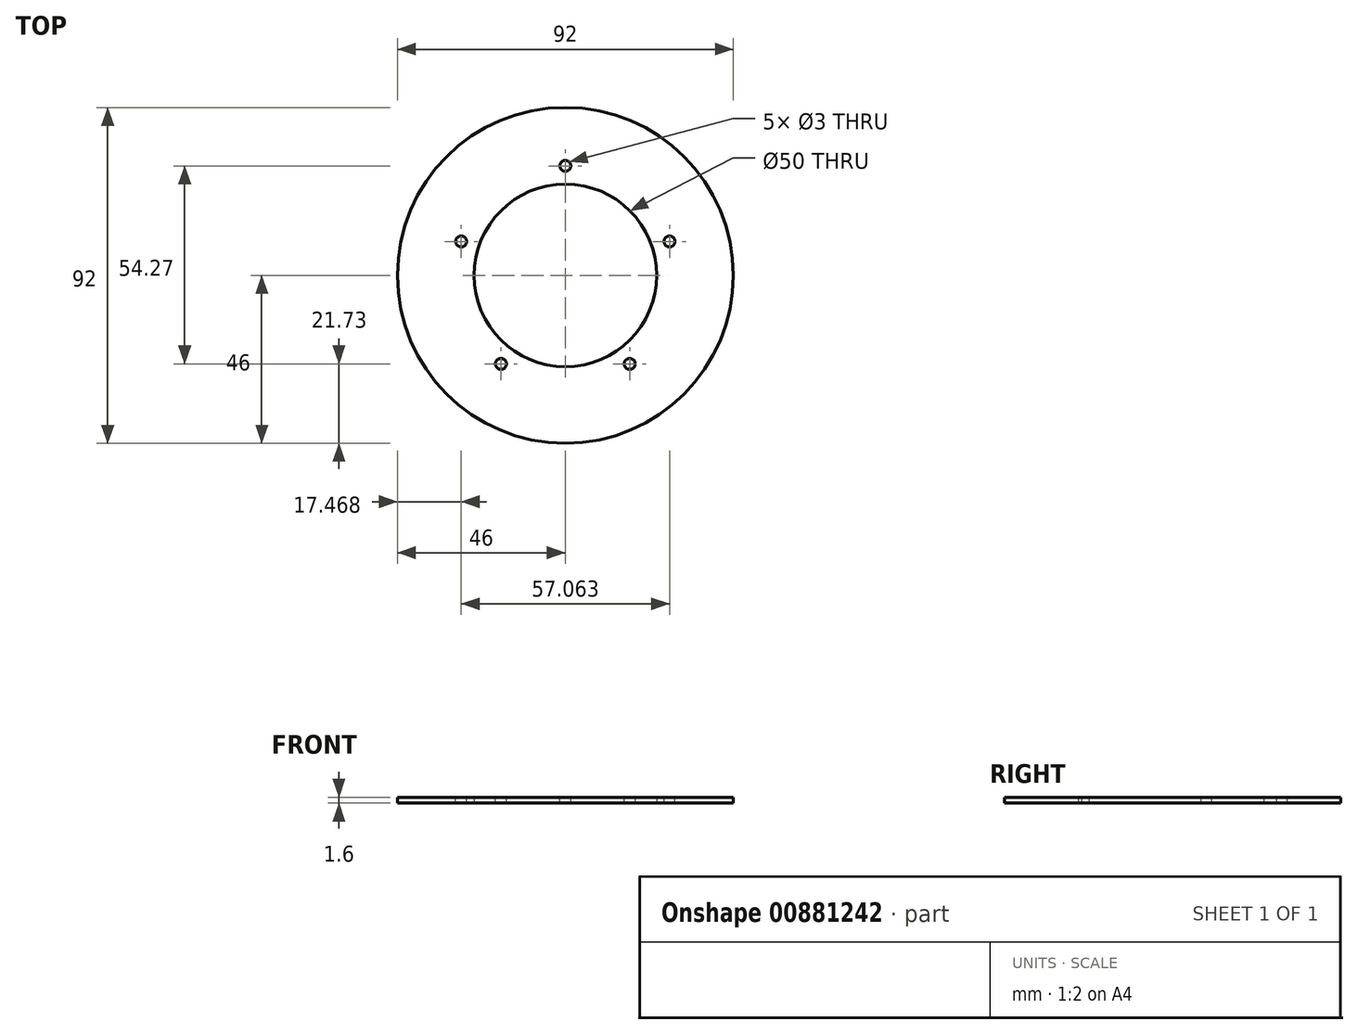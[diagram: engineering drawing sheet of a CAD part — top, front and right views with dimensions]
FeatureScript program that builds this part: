
annotation { "Feature Type Name" : "Feature", "Feature Type Description" : "" }
export const myFeature = defineFeature(function(context is Context, id is Id, definition is map)
    precondition{}
    {
        {
            var Q0;
            Q0=qCreatedBy(makeId("Top.planeOp"),FACE);
            var sketch = newSketch(context, id + "F0", { "sketchPlane" : qUnion([Q0])});
            skCircle(sketch, "E0", {"center": v(0, 0) * mm, "radius": 46 * mm});
            skCircle(sketch, "E1", {"center": v(0, 0) * mm, "radius": 25 * mm});
            skSolve(sketch);
        }
        {
            var Q0;
            Q0=qSketchRegion(id+"F0",true);
            extrude(context, id + "F1", {"entities" : qUnion([Q0]), "depth" : 1.6 * mm, "offsetDistance" : 25.4 * mm});
        }
        {
            var Q0;
            Q0=makeQuery(id+"F1.opExtrude","CAP_FACE",FACE,{"disambiguationData":[OSD([sQuery(id+"F0.wireOp",EDGE,"E0"),sQuery(id+"F0.wireOp",EDGE,"E1")])],"isStart":false});
            var sketch = newSketch(context, id + "F2", { "sketchPlane" : qUnion([Q0])});
            skCircle(sketch, "E2", {"center": v(0, 30) * mm, "radius": 1.5 * mm});
            skCircle(sketch, "E3.1.0", {"center": v(-28.53, 9.27) * mm, "radius": 1.5 * mm});
            skCircle(sketch, "E3.2.0", {"center": v(-17.63, -24.27) * mm, "radius": 1.5 * mm});
            skCircle(sketch, "E3.3.0", {"center": v(17.63, -24.27) * mm, "radius": 1.5 * mm});
            skCircle(sketch, "E3.4.0", {"center": v(28.53, 9.27) * mm, "radius": 1.5 * mm});
            skPoint(sketch, "E3.center", {"position": v(0, 0) * mm});
            skSolve(sketch);
        }
        {
            var Q0;
            Q0=qSketchRegion(id+"F2",true);
            extrude(context, id + "F3", {"entities" : qUnion([Q0]), "operationType" : NewBodyOperationType.REMOVE, "oppositeDirection" : true, "depth" : 25.4 * mm, "offsetDistance" : 25.4 * mm});
        }
    });
